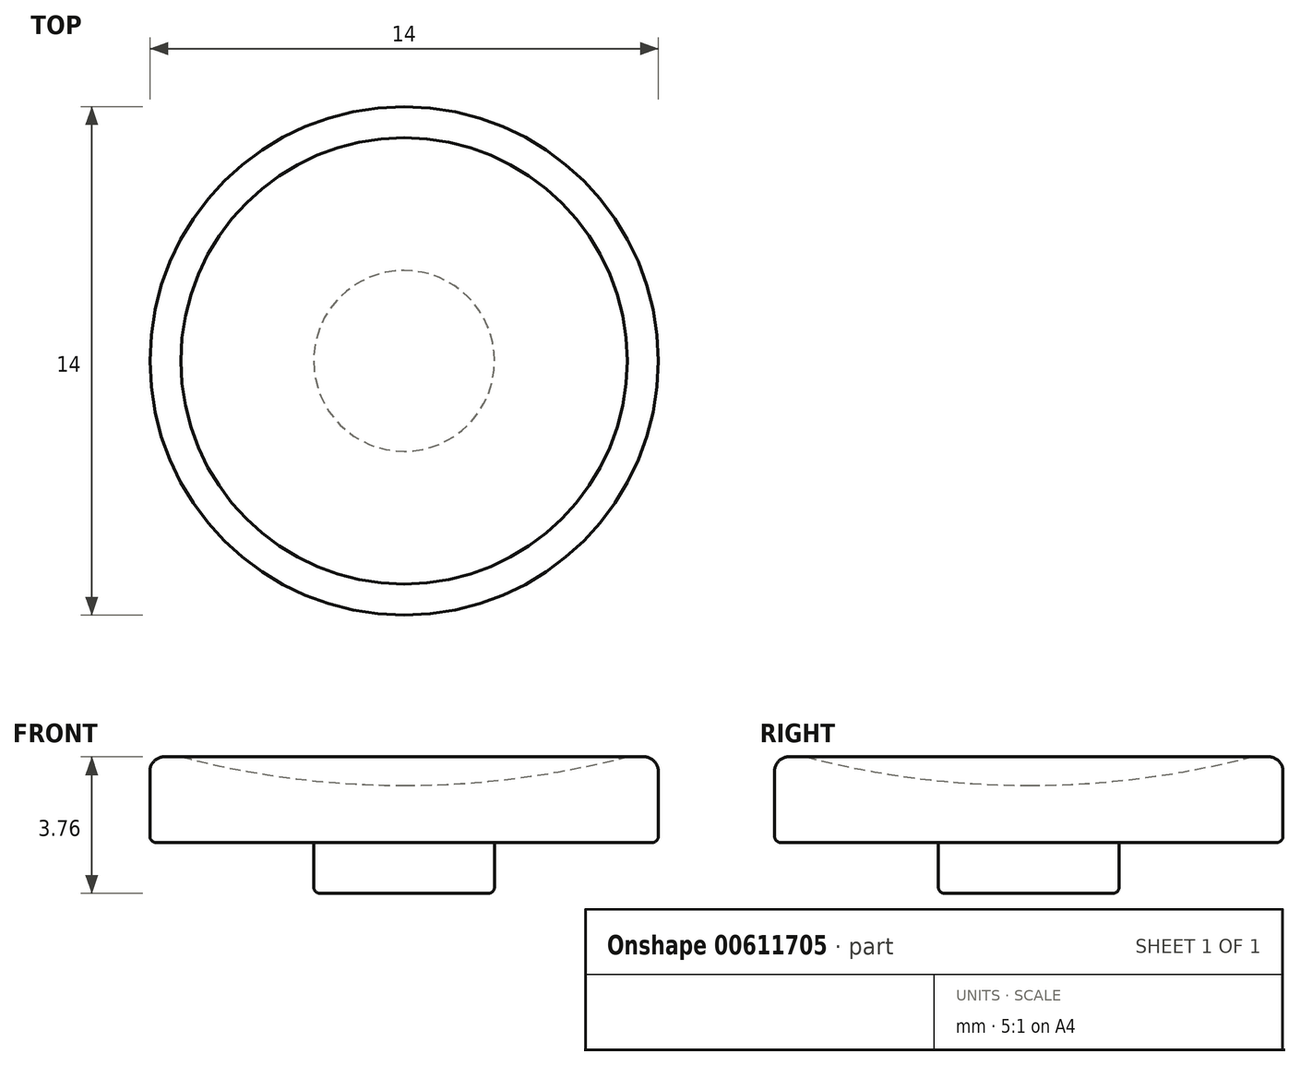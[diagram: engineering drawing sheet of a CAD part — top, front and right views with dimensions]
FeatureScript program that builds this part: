
annotation { "Feature Type Name" : "Feature", "Feature Type Description" : "" }
export const myFeature = defineFeature(function(context is Context, id is Id, definition is map)
    precondition{}
    {
        {
            var Q0;
            Q0=qCreatedBy(makeId("Front.planeOp"),FACE);
            var sketch = newSketch(context, id + "F0", { "sketchPlane" : qUnion([Q0])});
            skLineSegment(sketch, "E0.bottom", {"start": v(0, 0) * mm, "end": v(-7, 0) * mm});
            skLineSegment(sketch, "E0.left", {"start": v(0, 0) * mm, "end": v(0, 1.57) * mm});
            skLineSegment(sketch, "E0.right", {"start": v(-7, 0) * mm, "end": v(-7, 2.36) * mm});
            skArc(sketch, "E1", {"start": v(-6.14, 2.36) * mm, "mid": v(-3.1, 1.77) * mm, "end": v(0, 1.57) * mm});
            skLineSegment(sketch, "E2", {"start": v(-7, 2.36) * mm, "end": v(-6.14, 2.36) * mm});
            skSolve(sketch);
        }
        {
            var Q0;
            Q0=makeQuery(id+"F0.imprint","IMPRINT",FACE,{"disambiguationData":[TD([[makeQuery(id+"F0.imprint","IMPRINT",EDGE,{"derivedFrom":sQuery(id+"F0.wireOp",EDGE,"E0.bottom")}),-1.0]])]});
            var Q1;
            Q1=sQuery(id+"F0.wireOp",EDGE,"E0.left");
            revolve(context, id + "F1", {"entities" : qUnion([Q0]), "axis" : qUnion([Q1]), "revolveType" : RevolveType.FULL});
        }
        {
            var Q0;
            Q0=makeQuery(id+"F1.opRevolve","SWEPT_EDGE",EDGE,{"disambiguationData":[OSD([sQuery(id+"F0.wireOp",EDGE,"E0.right"),sQuery(id+"F0.wireOp",EDGE,"E2")])]});
            fillet(context, id + "F2", {"entities" : qUnion([Q0]), "radius" : .4 * mm, "tangentPropagation" : true, "allowEdgeOverflow" : false});
        }
        {
            var Q0;
            Q0=makeQuery(id+"F1.opRevolve","SWEPT_FACE",FACE,{"disambiguationData":[OSD([sQuery(id+"F0.wireOp",EDGE,"E0.bottom")])]});
            var sketch = newSketch(context, id + "F3", { "sketchPlane" : qUnion([Q0])});
            skCircle(sketch, "E3", {"center": v(0, 0) * mm, "radius": 2.5 * mm});
            skSolve(sketch);
        }
        {
            var Q0;
            Q0=qSketchRegion(id+"F3",true);
            extrude(context, id + "F4", {"entities" : qUnion([Q0]), "operationType" : NewBodyOperationType.ADD, "depth" : 1.4 * mm, "offsetDistance" : 25 * mm});
        }
        {
            var Q0;
            Q0=makeQuery(id+"F4.opExtrude","CAP_FACE",FACE,{"disambiguationData":[OSD([sQuery(id+"F3.wireOp",EDGE,"E3")])],"isStart":false});
            var Q1;
            Q1=makeQuery(id+"F4.opExtrude","CAP_EDGE",EDGE,{"disambiguationData":[OSD([sQuery(id+"F3.wireOp",EDGE,"E3")])],"isStart":true});
            var Q2;
            Q2=makeQuery(id+"F1.opRevolve","SWEPT_EDGE",EDGE,{"disambiguationData":[OSD([sQuery(id+"F0.wireOp",EDGE,"E0.bottom"),sQuery(id+"F0.wireOp",EDGE,"E0.right")])]});
            fillet(context, id + "F5", {"entities" : qUnion([Q0, Q1, Q2]), "radius" : .175 * mm, "tangentPropagation" : true, "allowEdgeOverflow" : false});
        }
    });
